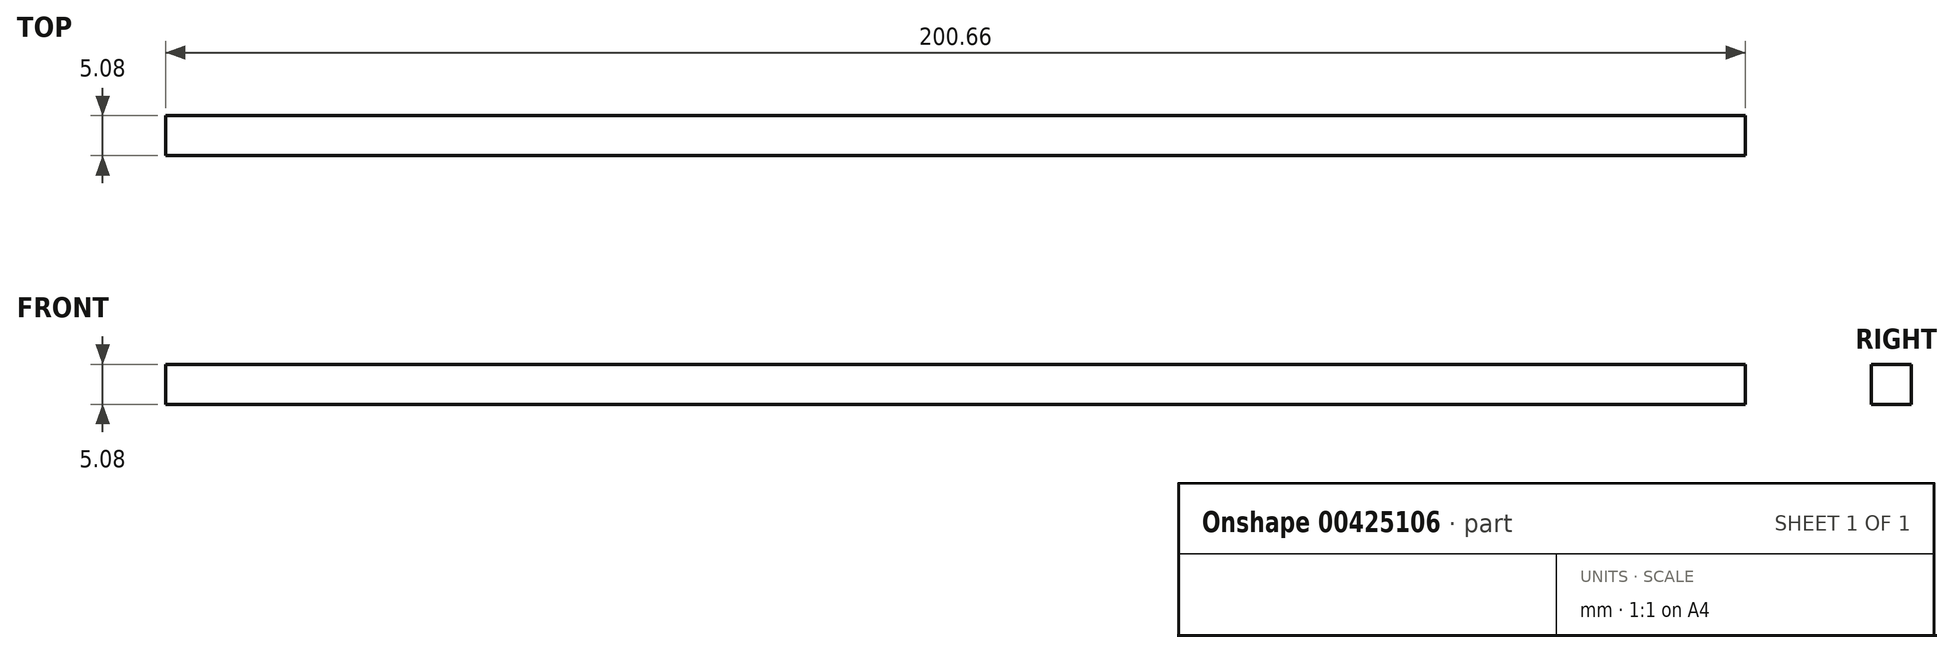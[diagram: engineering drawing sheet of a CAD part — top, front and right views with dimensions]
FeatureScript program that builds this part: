
annotation { "Feature Type Name" : "Feature", "Feature Type Description" : "" }
export const myFeature = defineFeature(function(context is Context, id is Id, definition is map)
    precondition{}
    {
        {
            var Q0;
            Q0=qCreatedBy(makeId("Front.planeOp"),FACE);
            var sketch = newSketch(context, id + "F0", { "sketchPlane" : qUnion([Q0])});
            skLineSegment(sketch, "E0.bottom", {"start": v(-99.63, -46.86) * mm, "end": v(101.03, -46.86) * mm});
            skLineSegment(sketch, "E0.top", {"start": v(-99.63, -41.78) * mm, "end": v(101.03, -41.78) * mm});
            skLineSegment(sketch, "E0.left", {"start": v(-99.63, -46.86) * mm, "end": v(-99.63, -41.78) * mm});
            skLineSegment(sketch, "E0.right", {"start": v(101.03, -46.86) * mm, "end": v(101.03, -41.78) * mm});
            skSolve(sketch);
        }
        {
            var Q0;
            Q0 = qSketchRegion(id + "F0", true);
            extrude(context, id + "F1", {"entities" : qUnion([Q0]), "depth" : 5.08 * mm});
        }
    });
